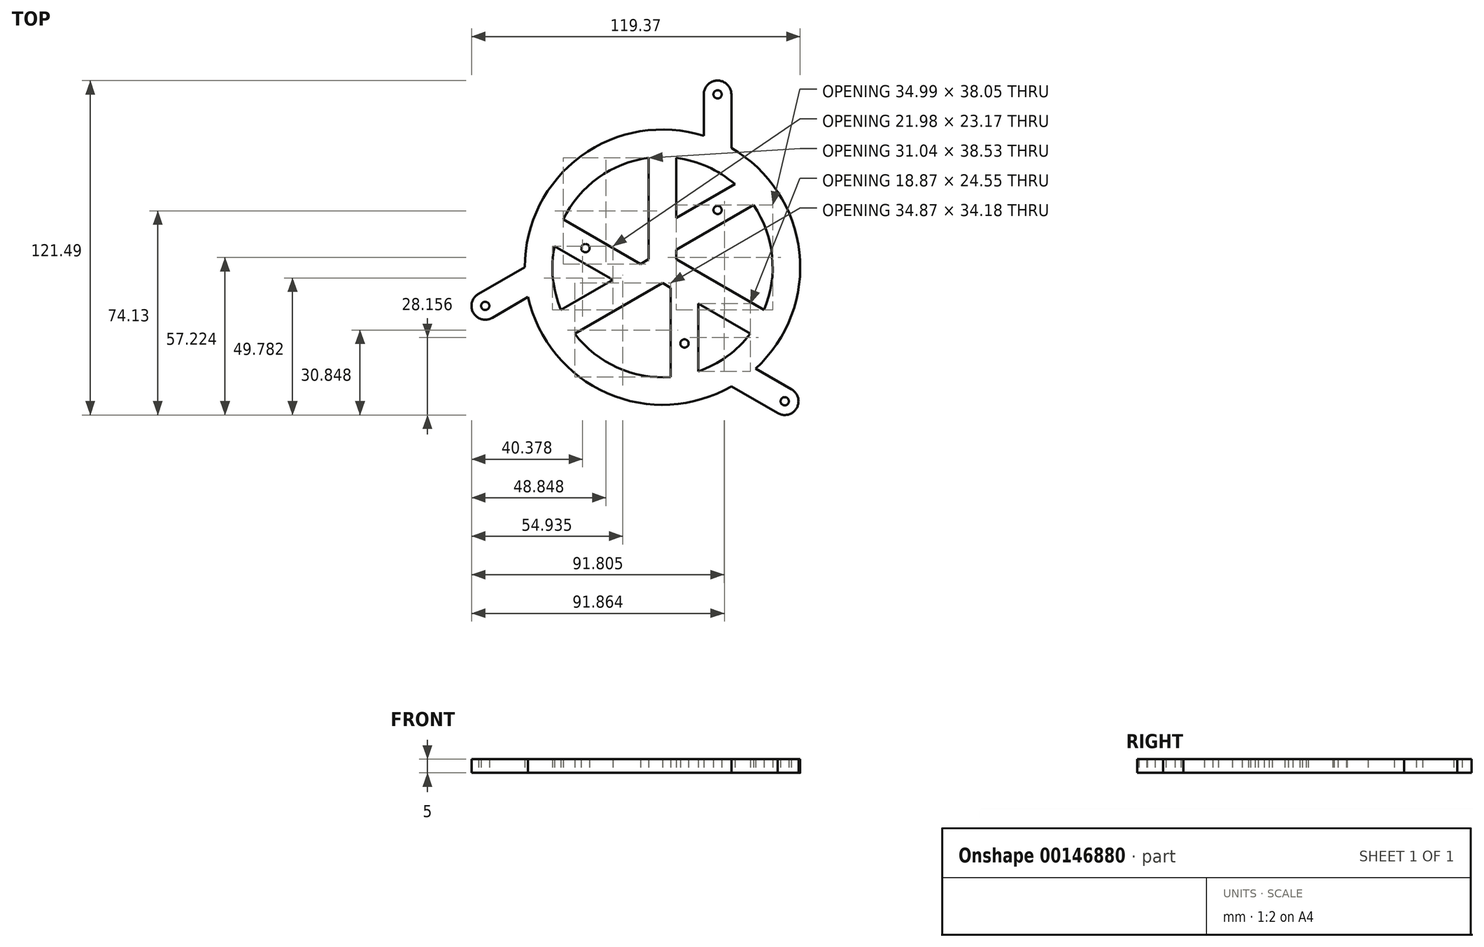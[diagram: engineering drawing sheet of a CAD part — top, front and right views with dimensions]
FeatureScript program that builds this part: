
annotation { "Feature Type Name" : "Feature", "Feature Type Description" : "" }
export const myFeature = defineFeature(function(context is Context, id is Id, definition is map)
    precondition{}
    {
        {
            var Q0;
            Q0=qCreatedBy(makeId("Top.planeOp"),FACE);
            var sketch = newSketch(context, id + "F0", { "sketchPlane" : qUnion([Q0])});
            skLineSegment(sketch, "E0", {"start": v(0, 0) * mm, "end": v(134.92, -77.9) * mm, "construction": true});
            skLineSegment(sketch, "E1", {"start": v(0, 0) * mm, "end": v(-133.4, -77.02) * mm, "construction": true});
            skLineSegment(sketch, "E2", {"start": v(-140.97, -58.3) * mm, "end": v(38.14, 45.11) * mm, "construction": true});
            skLineSegment(sketch, "E3", {"start": v(120.26, -92.52) * mm, "end": v(-72.64, 18.84) * mm, "construction": true});
            skLineSegment(sketch, "E4", {"start": v(20, 112.68) * mm, "end": v(20, -65.02) * mm, "construction": true});
            skCircle(sketch, "E5", {"center": v(20, 62.78) * mm, "radius": 1.5 * mm});
            skCircle(sketch, "E6", {"center": v(20, 20.78) * mm, "radius": 1.5 * mm});
            skCircle(sketch, "E7", {"center": v(44.37, -48.71) * mm, "radius": 1.5 * mm});
            skCircle(sketch, "E8", {"center": v(8, -27.71) * mm, "radius": 1.5 * mm});
            skCircle(sketch, "E9", {"center": v(-64.37, -14.07) * mm, "radius": 1.5 * mm});
            skCircle(sketch, "E10", {"center": v(-28, 6.93) * mm, "radius": 1.5 * mm});
            skArc(sketch, "E11", {"start": v(-66.75, -9.67) * mm, "mid": v(-68.73, -16.52) * mm, "end": v(-61.85, -18.39) * mm});
            skArc(sketch, "E12", {"start": v(41.75, -52.97) * mm, "mid": v(48.72, -51.2) * mm, "end": v(46.7, -44.3) * mm});
            skArc(sketch, "E13", {"start": v(25, 62.54) * mm, "mid": v(20.06, 67.78) * mm, "end": v(15, 62.66) * mm});
            skArc(sketch, "E14", {"start": v(33.8, -36.84) * mm, "mid": v(49.7, 5.46) * mm, "end": v(25, 43.3) * mm});
            skArc(sketch, "E15", {"start": v(-5, 39.69) * mm, "mid": v(-23.36, 32.47) * mm, "end": v(-36.04, 17.35) * mm});
            skLineSegment(sketch, "E16", {"start": v(-61.85, -18.39) * mm, "end": v(-48.8, -10.86) * mm});
            skLineSegment(sketch, "E17", {"start": v(-67, -9.82) * mm, "end": v(-50, 0) * mm});
            skLineSegment(sketch, "E18", {"start": v(15, 62.9) * mm, "end": v(15, 47.7) * mm});
            skLineSegment(sketch, "E19", {"start": v(25, 63.03) * mm, "end": v(25, 43.3) * mm});
            skLineSegment(sketch, "E20", {"start": v(46.7, -44.3) * mm, "end": v(33.8, -36.84) * mm});
            skLineSegment(sketch, "E21", {"start": v(41.75, -52.97) * mm, "end": v(25, -43.3) * mm});
            skArc(sketch, "E22.trimOffspring", {"start": v(15, 47.7) * mm, "mid": v(-29.58, 40.31) * mm, "end": v(-50, 0) * mm});
            skArc(sketch, "E23.trimOffspring", {"start": v(-48.8, -10.86) * mm, "mid": v(-20.12, -45.77) * mm, "end": v(25, -43.3) * mm});
            skLineSegment(sketch, "E24", {"start": v(-5, 39.69) * mm, "end": v(-5, 2.89) * mm});
            skLineSegment(sketch, "E25", {"start": v(-36.87, -15.51) * mm, "end": v(-18, -4.62) * mm});
            skLineSegment(sketch, "E26", {"start": v(5, 39.69) * mm, "end": v(5, 17.9) * mm});
            skLineSegment(sketch, "E27", {"start": v(36.87, -15.51) * mm, "end": v(5, 2.89) * mm});
            skLineSegment(sketch, "E28", {"start": v(31.87, -24.17) * mm, "end": v(13, -13.28) * mm});
            skLineSegment(sketch, "E29", {"start": v(0, -5.77) * mm, "end": v(-31.87, -24.17) * mm});
            skPoint(sketch, "E30.orphan", {"position": v(-5, 0) * mm});
            skArc(sketch, "E31.trimOffspring", {"start": v(-31.87, -24.17) * mm, "mid": v(-16.43, -36.47) * mm, "end": v(3, -39.89) * mm});
            skArc(sketch, "E32.trimOffspring", {"start": v(36.87, -15.51) * mm, "mid": v(39.8, 4) * mm, "end": v(33.04, 22.54) * mm});
            skLineSegment(sketch, "E33", {"start": v(-18, -4.62) * mm, "end": v(-39.26, 7.66) * mm});
            skLineSegment(sketch, "E34", {"start": v(-8, 1.15) * mm, "end": v(-36.04, 17.35) * mm});
            skLineSegment(sketch, "E35", {"start": v(5, 17.9) * mm, "end": v(26.26, 30.17) * mm});
            skLineSegment(sketch, "E36", {"start": v(5, 6.35) * mm, "end": v(33.04, 22.54) * mm});
            skLineSegment(sketch, "E37", {"start": v(13, -13.28) * mm, "end": v(13, -37.83) * mm});
            skLineSegment(sketch, "E38", {"start": v(3, -7.5) * mm, "end": v(3, -39.89) * mm});
            skArc(sketch, "E39.trimOffspring", {"start": v(26.26, 30.17) * mm, "mid": v(16.34, 36.51) * mm, "end": v(5, 39.69) * mm});
            skLineSegment(sketch, "E40.trimOffspring", {"start": v(5, 6.35) * mm, "end": v(5, 2.89) * mm});
            skLineSegment(sketch, "E41.trimOffspring", {"start": v(3, -7.5) * mm, "end": v(0, -5.77) * mm});
            skArc(sketch, "E42.trimOffspring", {"start": v(13, -37.83) * mm, "mid": v(23.45, -32.4) * mm, "end": v(31.87, -24.17) * mm});
            skLineSegment(sketch, "E43.trimOffspring", {"start": v(-8, 1.15) * mm, "end": v(-5, 2.89) * mm});
            skArc(sketch, "E44.trimOffspring", {"start": v(-39.26, 7.66) * mm, "mid": v(-39.79, -4.1) * mm, "end": v(-36.87, -15.51) * mm});
            skSolve(sketch);
        }
        {
            var Q0;
            Q0 = qSketchRegion(id + "F0", true);
            extrude(context, id + "F1", {"entities" : qUnion([Q0]), "depth" : 5 * mm});
        }
    });
